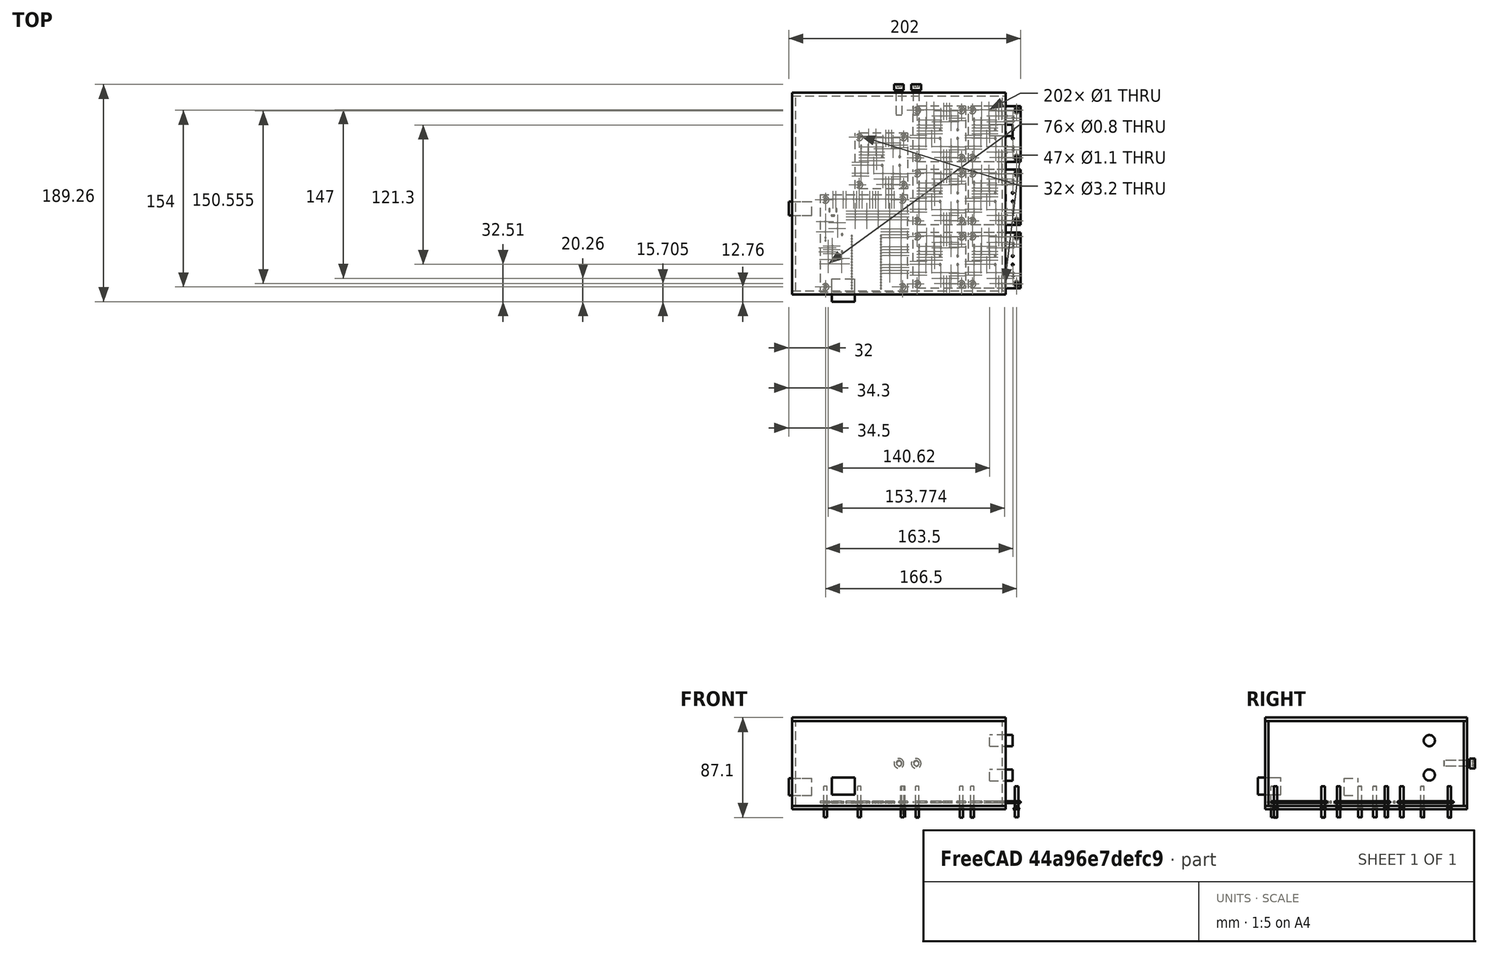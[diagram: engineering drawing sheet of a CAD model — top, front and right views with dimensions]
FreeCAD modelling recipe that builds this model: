
FCSTD DOCUMENT  (FreeCAD 0.20R29177 +426 (Git))
Label: electronics_enclosure
License: All rights reserved
LicenseURL: http://en.wikipedia.org/wiki/All_rights_reserved
objects: Part::Feature×74, Part::Cylinder×35, App::LinkGroup×15, Part::Compound×12, Part::FeaturePython×2, Part::Box×2, Part::MultiFuse×1
note: 126 computed .brp shape members not serialized (recipe doc carries the construction recipe); baked Part::Feature solids carry a one-line shape summary decoded from their .brp

FEATURE [Part::Feature] Pcb_e13b
  Placement = pos=(0,112.5,0) rot=(0,0,1;0rad)
  shape: bbox 45.5 x 48.5 x 1.6 mm, 54 faces (baked)
FEATURE [Part::Feature] Pcb_e13b001
  Placement = pos=(0,57.5,0) rot=(0,0,1;0rad)
  shape: bbox 45.5 x 48.5 x 1.6 mm, 54 faces (baked)
FEATURE [Part::Feature] Pcb_e13b002
  Placement = pos=(0,2.5,0) rot=(0,0,1;0rad)
  shape: bbox 45.5 x 48.5 x 1.6 mm, 54 faces (baked)
FEATURE [Part::Feature] Pcb_b27c
  Placement = pos=(242,-190,0) rot=(0,0,1;3.14159rad)
  shape: bbox 76 x 85 x 1.6 mm, 143 faces (baked)
FEATURE [Part::Compound] Compound  label="PCBs_Compound"
  Links = -> [Pcb_e13b,Pcb_e13b001,Pcb_e13b002,Pcb_b27c]
  Placement = pos=(-99.5,44,-33) rot=(0,0,1;0rad)
FEATURE [Part::Feature] BOLTS_part008  label="Hex socket countersunk head screw DIN 7991 M3 20.008"
  Placement = pos=(16,-79,-40) rot=(0,0,1;0rad)
  shape: bbox 6 x 6 x 20 mm, 12 faces (baked)
FEATURE [Part::Feature] BOLTS_part009  label="Hex socket countersunk head screw DIN 7991 M3 20.009"
  Placement = pos=(16,-37.5,-40) rot=(0,0,1;0rad)
  shape: bbox 6 x 6 x 20 mm, 12 faces (baked)
FEATURE [Part::Feature] BOLTS_part010  label="Hex socket countersunk head screw DIN 7991 M3 20.010"
  Placement = pos=(54.5,-37.5,-40) rot=(0,0,1;0rad)
  shape: bbox 6 x 6 x 20 mm, 12 faces (baked)
FEATURE [Part::Feature] BOLTS_part011  label="Hex socket countersunk head screw DIN 7991 M3 20.011"
  Placement = pos=(54.5,-79,-40) rot=(0,0,1;0rad)
  shape: bbox 6 x 6 x 20 mm, 12 faces (baked)
FEATURE [Part::Compound] Compound003  label="sol_driver_screw_Compound002"
  Links = -> [BOLTS_part008,BOLTS_part009,BOLTS_part010,BOLTS_part011]
FEATURE [Part::Feature] BOLTS_part012  label="Hex socket countersunk head screw DIN 7991 M3 20.012"
  Placement = pos=(16,-79,-40) rot=(0,0,1;0rad)
  shape: bbox 6 x 6 x 20 mm, 12 faces (baked)
FEATURE [Part::Feature] BOLTS_part013  label="Hex socket countersunk head screw DIN 7991 M3 20.013"
  Placement = pos=(16,-37.5,-40) rot=(0,0,1;0rad)
  shape: bbox 6 x 6 x 20 mm, 12 faces (baked)
FEATURE [Part::Feature] BOLTS_part014  label="Hex socket countersunk head screw DIN 7991 M3 20.014"
  Placement = pos=(54.5,-37.5,-40) rot=(0,0,1;0rad)
  shape: bbox 6 x 6 x 20 mm, 12 faces (baked)
FEATURE [Part::Feature] BOLTS_part015  label="Hex socket countersunk head screw DIN 7991 M3 20.015"
  Placement = pos=(54.5,-79,-40) rot=(0,0,1;0rad)
  shape: bbox 6 x 6 x 20 mm, 12 faces (baked)
FEATURE [Part::Feature] BOLTS_part016  label="Hex socket countersunk head screw DIN 7991 M3 20.016"
  Placement = pos=(16,-79,-40) rot=(0,0,1;0rad)
  shape: bbox 6 x 6 x 20 mm, 12 faces (baked)
FEATURE [Part::Feature] BOLTS_part017  label="Hex socket countersunk head screw DIN 7991 M3 20.017"
  Placement = pos=(16,-37.5,-40) rot=(0,0,1;0rad)
  shape: bbox 6 x 6 x 20 mm, 12 faces (baked)
FEATURE [Part::Feature] BOLTS_part018  label="Hex socket countersunk head screw DIN 7991 M3 20.018"
  Placement = pos=(54.5,-37.5,-40) rot=(0,0,1;0rad)
  shape: bbox 6 x 6 x 20 mm, 12 faces (baked)
FEATURE [Part::Feature] BOLTS_part019  label="Hex socket countersunk head screw DIN 7991 M3 20.019"
  Placement = pos=(54.5,-79,-40) rot=(0,0,1;0rad)
  shape: bbox 6 x 6 x 20 mm, 12 faces (baked)
FEATURE [Part::Feature] BOLTS_part020  label="Hex socket countersunk head screw DIN 7991 M3 20.020"
  Placement = pos=(16,-79,-40) rot=(0,0,1;0rad)
  shape: bbox 6 x 6 x 20 mm, 12 faces (baked)
FEATURE [Part::Feature] BOLTS_part021  label="Hex socket countersunk head screw DIN 7991 M3 20.021"
  Placement = pos=(16,-37.5,-40) rot=(0,0,1;0rad)
  shape: bbox 6 x 6 x 20 mm, 12 faces (baked)
FEATURE [Part::Feature] BOLTS_part022  label="Hex socket countersunk head screw DIN 7991 M3 20.022"
  Placement = pos=(54.5,-37.5,-40) rot=(0,0,1;0rad)
  shape: bbox 6 x 6 x 20 mm, 12 faces (baked)
FEATURE [Part::Feature] BOLTS_part023  label="Hex socket countersunk head screw DIN 7991 M3 20.023"
  Placement = pos=(54.5,-79,-40) rot=(0,0,1;0rad)
  shape: bbox 6 x 6 x 20 mm, 12 faces (baked)
FEATURE [Part::Compound] Compound005  label="sol_driver_screw_Compound003"
  Links = -> [BOLTS_part012,BOLTS_part013,BOLTS_part014,BOLTS_part015]
  Placement = pos=(0,110,0) rot=(0,0,1;0rad)
FEATURE [Part::Compound] Compound006  label="sol_driver_screw_Compound004"
  Links = -> [BOLTS_part016,BOLTS_part017,BOLTS_part018,BOLTS_part019]
  Placement = pos=(0,55,0) rot=(0,0,1;0rad)
FEATURE [Part::Compound] Compound007  label="sol_driver_screw_Compound005"
  Links = -> [BOLTS_part020,BOLTS_part021,BOLTS_part022,BOLTS_part023]
FEATURE [Part::Feature] Pcb_e13b003
  Placement = pos=(0,112.5,0) rot=(0,0,1;0rad)
  shape: bbox 45.5 x 48.5 x 1.6 mm, 54 faces (baked)
FEATURE [Part::Feature] Pcb_e13b004
  Placement = pos=(0,57.5,0) rot=(0,0,1;0rad)
  shape: bbox 45.5 x 48.5 x 1.6 mm, 54 faces (baked)
FEATURE [Part::Feature] Pcb_e13b005
  Placement = pos=(0,2.5,0) rot=(0,0,1;0rad)
  shape: bbox 45.5 x 48.5 x 1.6 mm, 54 faces (baked)
FEATURE [Part::Compound] Compound004  label="PCBs_Compound001"
  Links = -> [Pcb_e13b003,Pcb_e13b004,Pcb_e13b005]
  Placement = pos=(-99.5,44,-33) rot=(0,0,1;0rad)
FEATURE [Part::Compound] Compound008
  Links = -> [Compound007,Compound004,Compound005,Compound006]
  Placement = pos=(48,0,0) rot=(0,0,1;0rad)
FEATURE [Part::Feature] BOLTS_part004  label="Hex socket countersunk head screw DIN 7991 M3 20.004"
  Placement = pos=(16,-79,-40) rot=(0,0,1;0rad)
  shape: bbox 6 x 6 x 20 mm, 12 faces (baked)
FEATURE [Part::Feature] BOLTS_part005  label="Hex socket countersunk head screw DIN 7991 M3 20.005"
  Placement = pos=(16,-37.5,-40) rot=(0,0,1;0rad)
  shape: bbox 6 x 6 x 20 mm, 12 faces (baked)
FEATURE [Part::Feature] BOLTS_part006  label="Hex socket countersunk head screw DIN 7991 M3 20.006"
  Placement = pos=(54.5,-37.5,-40) rot=(0,0,1;0rad)
  shape: bbox 6 x 6 x 20 mm, 12 faces (baked)
FEATURE [Part::Feature] BOLTS_part007  label="Hex socket countersunk head screw DIN 7991 M3 20.007"
  Placement = pos=(54.5,-79,-40) rot=(0,0,1;0rad)
  shape: bbox 6 x 6 x 20 mm, 12 faces (baked)
FEATURE [Part::Compound] Compound002  label="sol_driver_screw_Compound001"
  Links = -> [BOLTS_part004,BOLTS_part005,BOLTS_part006,BOLTS_part007]
  Placement = pos=(0,55,0) rot=(0,0,1;0rad)
FEATURE [Part::Feature] BOLTS_part003  label="Hex socket countersunk head screw DIN 7991 M3 20.003"
  Placement = pos=(54.5,-79,-40) rot=(0,0,1;0rad)
  shape: bbox 6 x 6 x 20 mm, 12 faces (baked)
FEATURE [Part::Feature] BOLTS_part002  label="Hex socket countersunk head screw DIN 7991 M3 20.002"
  Placement = pos=(54.5,-37.5,-40) rot=(0,0,1;0rad)
  shape: bbox 6 x 6 x 20 mm, 12 faces (baked)
FEATURE [Part::Feature] BOLTS_part001  label="Hex socket countersunk head screw DIN 7991 M3 20.001"
  Placement = pos=(16,-37.5,-40) rot=(0,0,1;0rad)
  shape: bbox 6 x 6 x 20 mm, 12 faces (baked)
FEATURE [Part::Feature] BOLTS_part  label="Hex socket countersunk head screw DIN 7991 M3 20.0"
  Placement = pos=(16,-79,-40) rot=(0,0,1;0rad)
  shape: bbox 6 x 6 x 20 mm, 12 faces (baked)
FEATURE [Part::Compound] Compound001  label="sol_driver_screw_Compound"
  Links = -> [BOLTS_part,BOLTS_part001,BOLTS_part002,BOLTS_part003]
  Placement = pos=(0,110,0) rot=(0,0,1;0rad)
FEATURE [Part::Feature] BOLTS_part024  label="Hex socket countersunk head screw DIN 7991 M3 20.024"
  Placement = pos=(16,-79,-40) rot=(0,0,1;0rad)
  shape: bbox 6 x 6 x 20 mm, 12 faces (baked)
FEATURE [Part::Feature] BOLTS_part025  label="Hex socket countersunk head screw DIN 7991 M3 20.025"
  Placement = pos=(16,-37.5,-40) rot=(0,0,1;0rad)
  shape: bbox 6 x 6 x 20 mm, 12 faces (baked)
FEATURE [Part::Feature] BOLTS_part026  label="Hex socket countersunk head screw DIN 7991 M3 20.026"
  Placement = pos=(54.5,-37.5,-40) rot=(0,0,1;0rad)
  shape: bbox 6 x 6 x 20 mm, 12 faces (baked)
FEATURE [Part::Feature] BOLTS_part027  label="Hex socket countersunk head screw DIN 7991 M3 20.027"
  Placement = pos=(54.5,-79,-40) rot=(0,0,1;0rad)
  shape: bbox 6 x 6 x 20 mm, 12 faces (baked)
FEATURE [Part::Compound] Compound009  label="sol_driver_screw_Compound006"
  Links = -> [BOLTS_part024,BOLTS_part025,BOLTS_part026,BOLTS_part027]
FEATURE [Part::Feature] BOLTS_part028  label="Hex socket countersunk head screw DIN 7991 M3 20.028"
  Placement = pos=(3,-81.5,-53) rot=(0,0,1;0rad)
  shape: bbox 6 x 6 x 20 mm, 12 faces (baked)
FEATURE [Part::Feature] BOLTS_part029  label="Hex socket countersunk head screw DIN 7991 M3 20.029"
  Placement = pos=(3,-5.5,-53) rot=(0,0,1;0rad)
  shape: bbox 6 x 6 x 20 mm, 12 faces (baked)
FEATURE [Part::Feature] BOLTS_part030  label="Hex socket countersunk head screw DIN 7991 M3 20.030"
  Placement = pos=(-64,-81.5,-53) rot=(0,0,1;0rad)
  shape: bbox 6 x 6 x 20 mm, 12 faces (baked)
FEATURE [Part::Feature] BOLTS_part031  label="Hex socket countersunk head screw DIN 7991 M3 20.031"
  Placement = pos=(-64,-5.5,-53) rot=(0,0,1;0rad)
  shape: bbox 6 x 6 x 20 mm, 12 faces (baked)
FEATURE [Part::Compound] Compound010
  Links = -> [BOLTS_part028,BOLTS_part029,BOLTS_part030,BOLTS_part031]
  Placement = pos=(0,0,13) rot=(0,0,1;0rad)
FEATURE [Part::Feature] Pcb_e13b006
  Placement = pos=(-150,133,-33) rot=(0,0,1;0rad)
  shape: bbox 45.5 x 48.5 x 1.6 mm, 54 faces (baked)
FEATURE [Part::Feature] BOLTS_part032  label="Hex socket countersunk head screw DIN 7991 M3 20.032"
  Placement = pos=(16,-79,-40) rot=(0,0,1;0rad)
  shape: bbox 6 x 6 x 20 mm, 12 faces (baked)
FEATURE [Part::Feature] BOLTS_part033  label="Hex socket countersunk head screw DIN 7991 M3 20.033"
  Placement = pos=(16,-37.5,-40) rot=(0,0,1;0rad)
  shape: bbox 6 x 6 x 20 mm, 12 faces (baked)
FEATURE [Part::Feature] BOLTS_part034  label="Hex socket countersunk head screw DIN 7991 M3 20.034"
  Placement = pos=(54.5,-37.5,-40) rot=(0,0,1;0rad)
  shape: bbox 6 x 6 x 20 mm, 12 faces (baked)
FEATURE [Part::Feature] BOLTS_part035  label="Hex socket countersunk head screw DIN 7991 M3 20.035"
  Placement = pos=(54.5,-79,-40) rot=(0,0,1;0rad)
  shape: bbox 6 x 6 x 20 mm, 12 faces (baked)
FEATURE [Part::Compound] Compound011  label="sol_driver_screw_Compound007"
  Links = -> [BOLTS_part032,BOLTS_part033,BOLTS_part034,BOLTS_part035]
  Placement = pos=(-50.5,86.5,0) rot=(0,0,1;0rad)
FEATURE [Part::Feature] face_panel
  shape: bbox 186 x 3 x 74 mm, 6 faces (baked)
FEATURE [Part::Feature] behind_panel
  Placement = pos=(0,-173,0) rot=(0,0,1;0rad)
  shape: bbox 186 x 3 x 74 mm, 6 faces (baked)
FEATURE [Part::Feature] left_panel
  shape: bbox 3 x 170 x 74 mm, 6 faces (baked)
FEATURE [Part::Feature] right_panel
  Placement = pos=(-183,0,0) rot=(0,0,1;0rad)
  shape: bbox 3 x 170 x 74 mm, 6 faces (baked)
FEATURE [Part::Feature] bottom_panel
  shape: bbox 186 x 176 x 3 mm, 6 faces (baked)
FEATURE [Part::Feature] top_panel
  shape: bbox 186 x 176 x 3 mm, 6 faces (baked)
FEATURE [Part::FeaturePython] Box  # WARN: FeaturePython — macro-defined, semantics opaque (R4)
  parts = -> [face_panel,behind_panel,left_panel,right_panel,bottom_panel,top_panel]
FEATURE [Part::Box] Box001  label="Cube"
  AttacherType = Attacher::AttachEngine3D
  Height = 15
  Length = 20
  Placement = pos=(-58.5,-94.26,-27.17) rot=(0,0,1;0rad)
  Width = 20
FEATURE [Part::Box] Box002  label="Cube001"
  AttacherType = Attacher::AttachEngine3D
  Height = 15
  Length = 20
  Placement = pos=(-96,-19,-28) rot=(0,0,1;0rad)
  Width = 12
FEATURE [Part::Feature] BOLTS_part036  label="Hex socket head cap screw DIN 912 M5 20.0"
  Placement = pos=(15,95,0) rot=(1,0,0;1.5708rad)
  shape: bbox 8.5 x 27 x 8.5 mm, 12 faces (baked)
FEATURE [Part::Feature] BOLTS_part037  label="Hex socket head cap screw DIN 912 M5 20.001"
  Placement = pos=(0,95,0) rot=(1,0,0;1.5708rad)
  shape: bbox 8.5 x 27 x 8.5 mm, 12 faces (baked)
FEATURE [App::LinkGroup] LinkGroup001  label="banana_plugs1"
  ElementList = -> [BOLTS_part036,BOLTS_part037]
  LinkMode = 0
FEATURE [Part::Feature] BOLTS_part038  label="Hex socket head cap screw DIN 912 M5 20.002"
  Placement = pos=(15,95,0) rot=(1,0,0;1.5708rad)
  shape: bbox 8.5 x 27 x 8.5 mm, 12 faces (baked)
FEATURE [Part::Feature] BOLTS_part039  label="Hex socket head cap screw DIN 912 M5 20.003"
  Placement = pos=(0,95,0) rot=(1,0,0;1.5708rad)
  shape: bbox 8.5 x 27 x 8.5 mm, 12 faces (baked)
FEATURE [App::LinkGroup] LinkGroup002  label="banana_plugs002"
  ElementList = -> [BOLTS_part038,BOLTS_part039]
  LinkMode = 0
  Placement = pos=(35,0,0) rot=(0,0,1;0rad)
FEATURE [Part::Feature] BOLTS_part040  label="Hex socket head cap screw DIN 912 M5 20.004"
  Placement = pos=(15,95,0) rot=(1,0,0;1.5708rad)
  shape: bbox 8.5 x 27 x 8.5 mm, 12 faces (baked)
FEATURE [Part::Feature] BOLTS_part041  label="Hex socket head cap screw DIN 912 M5 20.005"
  Placement = pos=(0,95,0) rot=(1,0,0;1.5708rad)
  shape: bbox 8.5 x 27 x 8.5 mm, 12 faces (baked)
FEATURE [App::LinkGroup] LinkGroup003  label="banana_plugs003"
  ElementList = -> [BOLTS_part040,BOLTS_part041]
  LinkMode = 0
  Placement = pos=(35,0,-13) rot=(0,0,1;0rad)
FEATURE [Part::Feature] BOLTS_part042  label="Hex socket head cap screw DIN 912 M5 20.006"
  Placement = pos=(15,95,0) rot=(1,0,0;1.5708rad)
  shape: bbox 8.5 x 27 x 8.5 mm, 12 faces (baked)
FEATURE [Part::Feature] BOLTS_part043  label="Hex socket head cap screw DIN 912 M5 20.007"
  Placement = pos=(0,95,0) rot=(1,0,0;1.5708rad)
  shape: bbox 8.5 x 27 x 8.5 mm, 12 faces (baked)
FEATURE [App::LinkGroup] LinkGroup004  label="banana_plugs004"
  ElementList = -> [BOLTS_part042,BOLTS_part043]
  LinkMode = 0
  Placement = pos=(0,0,-13) rot=(0,0,1;0rad)
FEATURE [Part::Feature] BOLTS_part044  label="Hex socket head cap screw DIN 912 M5 20.008"
  Placement = pos=(15,95,0) rot=(1,0,0;1.5708rad)
  shape: bbox 8.5 x 27 x 8.5 mm, 12 faces (baked)
FEATURE [Part::Feature] BOLTS_part045  label="Hex socket head cap screw DIN 912 M5 20.009"
  Placement = pos=(0,95,0) rot=(1,0,0;1.5708rad)
  shape: bbox 8.5 x 27 x 8.5 mm, 12 faces (baked)
FEATURE [App::LinkGroup] LinkGroup005  label="banana_plugs005"
  ElementList = -> [BOLTS_part044,BOLTS_part045]
  LinkMode = 0
  Placement = pos=(-35,0,0) rot=(0,0,1;0rad)
FEATURE [Part::Feature] BOLTS_part046  label="Hex socket head cap screw DIN 912 M5 20.010"
  Placement = pos=(15,95,0) rot=(1,0,0;1.5708rad)
  shape: bbox 8.5 x 27 x 8.5 mm, 12 faces (baked)
FEATURE [Part::Feature] BOLTS_part047  label="Hex socket head cap screw DIN 912 M5 20.011"
  Placement = pos=(0,95,0) rot=(1,0,0;1.5708rad)
  shape: bbox 8.5 x 27 x 8.5 mm, 12 faces (baked)
FEATURE [App::LinkGroup] LinkGroup006  label="banana_plugs006"
  ElementList = -> [BOLTS_part046,BOLTS_part047]
  LinkMode = 0
  Placement = pos=(-35,0,-13) rot=(0,0,1;0rad)
FEATURE [App::LinkGroup] LinkGroup007
  ElementList = -> [LinkGroup001,LinkGroup002,LinkGroup003,LinkGroup004,LinkGroup005,LinkGroup006]
  LinkMode = 0
  Placement = pos=(4,-10,26) rot=(0,0,1;-1.5708rad)
FEATURE [Part::Feature] BOLTS_part048  label="Hex socket head cap screw DIN 912 M5 20.012"
  Placement = pos=(15,95,0) rot=(1,0,0;1.5708rad)
  shape: bbox 8.5 x 27 x 8.5 mm, 12 faces (baked)
FEATURE [Part::Feature] BOLTS_part049  label="Hex socket head cap screw DIN 912 M5 20.013"
  Placement = pos=(0,95,0) rot=(1,0,0;1.5708rad)
  shape: bbox 8.5 x 27 x 8.5 mm, 12 faces (baked)
FEATURE [Part::Feature] BOLTS_part050  label="Hex socket head cap screw DIN 912 M5 20.014"
  Placement = pos=(15,95,0) rot=(1,0,0;1.5708rad)
  shape: bbox 8.5 x 27 x 8.5 mm, 12 faces (baked)
FEATURE [Part::Feature] BOLTS_part051  label="Hex socket head cap screw DIN 912 M5 20.015"
  Placement = pos=(0,95,0) rot=(1,0,0;1.5708rad)
  shape: bbox 8.5 x 27 x 8.5 mm, 12 faces (baked)
FEATURE [Part::Feature] BOLTS_part052  label="Hex socket head cap screw DIN 912 M5 20.016"
  Placement = pos=(15,95,0) rot=(1,0,0;1.5708rad)
  shape: bbox 8.5 x 27 x 8.5 mm, 12 faces (baked)
FEATURE [Part::Feature] BOLTS_part053  label="Hex socket head cap screw DIN 912 M5 20.017"
  Placement = pos=(0,95,0) rot=(1,0,0;1.5708rad)
  shape: bbox 8.5 x 27 x 8.5 mm, 12 faces (baked)
FEATURE [Part::Feature] BOLTS_part054  label="Hex socket head cap screw DIN 912 M5 20.018"
  Placement = pos=(15,95,0) rot=(1,0,0;1.5708rad)
  shape: bbox 8.5 x 27 x 8.5 mm, 12 faces (baked)
FEATURE [Part::Feature] BOLTS_part055  label="Hex socket head cap screw DIN 912 M5 20.019"
  Placement = pos=(0,95,0) rot=(1,0,0;1.5708rad)
  shape: bbox 8.5 x 27 x 8.5 mm, 12 faces (baked)
FEATURE [Part::Feature] BOLTS_part056  label="Hex socket head cap screw DIN 912 M5 20.020"
  Placement = pos=(15,95,0) rot=(1,0,0;1.5708rad)
  shape: bbox 8.5 x 27 x 8.5 mm, 12 faces (baked)
FEATURE [Part::Feature] BOLTS_part057  label="Hex socket head cap screw DIN 912 M5 20.021"
  Placement = pos=(0,95,0) rot=(1,0,0;1.5708rad)
  shape: bbox 8.5 x 27 x 8.5 mm, 12 faces (baked)
FEATURE [Part::Feature] BOLTS_part058  label="Hex socket head cap screw DIN 912 M5 20.022"
  Placement = pos=(15,95,0) rot=(1,0,0;1.5708rad)
  shape: bbox 8.5 x 27 x 8.5 mm, 12 faces (baked)
FEATURE [Part::Feature] BOLTS_part059  label="Hex socket head cap screw DIN 912 M5 20.023"
  Placement = pos=(0,95,0) rot=(1,0,0;1.5708rad)
  shape: bbox 8.5 x 27 x 8.5 mm, 12 faces (baked)
FEATURE [App::LinkGroup] LinkGroup008  label="banana_plugs007"
  ElementList = -> [BOLTS_part048,BOLTS_part049]
  LinkMode = 0
FEATURE [App::LinkGroup] LinkGroup009  label="banana_plugs008"
  ElementList = -> [BOLTS_part050,BOLTS_part051]
  LinkMode = 0
  Placement = pos=(35,0,0) rot=(0,0,1;0rad)
FEATURE [App::LinkGroup] LinkGroup010  label="banana_plugs009"
  ElementList = -> [BOLTS_part052,BOLTS_part053]
  LinkMode = 0
  Placement = pos=(35,0,-13) rot=(0,0,1;0rad)
FEATURE [App::LinkGroup] LinkGroup011  label="banana_plugs010"
  ElementList = -> [BOLTS_part054,BOLTS_part055]
  LinkMode = 0
  Placement = pos=(0,0,-13) rot=(0,0,1;0rad)
FEATURE [App::LinkGroup] LinkGroup012  label="banana_plugs011"
  ElementList = -> [BOLTS_part056,BOLTS_part057]
  LinkMode = 0
  Placement = pos=(-35,0,0) rot=(0,0,1;0rad)
FEATURE [App::LinkGroup] LinkGroup013  label="banana_plugs012"
  ElementList = -> [BOLTS_part058,BOLTS_part059]
  LinkMode = 0
  Placement = pos=(-35,0,-13) rot=(0,0,1;0rad)
FEATURE [App::LinkGroup] LinkGroup014
  ElementList = -> [LinkGroup008,LinkGroup009,LinkGroup010,LinkGroup011,LinkGroup012,LinkGroup013]
  LinkMode = 0
  Placement = pos=(4,-10,-4) rot=(0,0,1;-1.5708rad)
FEATURE [Part::Cylinder] Cylinder
  Angle = 360
  AttacherType = Attacher::AttachEngine3D
  FirstAngle = 0
  Height = 20
  Placement = pos=(79,55,-10.12) rot=(0,1,0;1.5708rad)
  Radius = 4.88
  SecondAngle = 0
FEATURE [Part::Cylinder] Cylinder001
  Angle = 360
  AttacherType = Attacher::AttachEngine3D
  FirstAngle = 0
  Height = 20
  Placement = pos=(79,55,19.88) rot=(0,1,0;1.5708rad)
  Radius = 4.88
  SecondAngle = 0
FEATURE [Part::Cylinder] Cylinder002
  Angle = 360
  AttacherType = Attacher::AttachEngine3D
  FirstAngle = 0
  Height = 10
  Placement = pos=(82,74.5,-47) rot=(0,0,1;0rad)
  Radius = 1.5
  SecondAngle = 0
FEATURE [Part::Cylinder] Cylinder004
  Angle = 360
  AttacherType = Attacher::AttachEngine3D
  FirstAngle = 0
  Height = 10
  Placement = pos=(82,33,-47) rot=(0,0,1;0rad)
  Radius = 1.5
  SecondAngle = 0
FEATURE [Part::Cylinder] Cylinder005
  Angle = 360
  AttacherType = Attacher::AttachEngine3D
  FirstAngle = 0
  Height = 10
  Placement = pos=(43.5,33,-47) rot=(0,0,1;0rad)
  Radius = 1.5
  SecondAngle = 0
FEATURE [Part::Cylinder] Cylinder006
  Angle = 360
  AttacherType = Attacher::AttachEngine3D
  FirstAngle = 0
  Height = 10
  Placement = pos=(82,19.5,-47) rot=(0,0,1;0rad)
  Radius = 1.5
  SecondAngle = 0
FEATURE [Part::Cylinder] Cylinder007
  Angle = 360
  AttacherType = Attacher::AttachEngine3D
  FirstAngle = 0
  Height = 10
  Placement = pos=(43.5,19.5,-47) rot=(0,0,1;0rad)
  Radius = 1.5
  SecondAngle = 0
FEATURE [Part::Cylinder] Cylinder008
  Angle = 360
  AttacherType = Attacher::AttachEngine3D
  FirstAngle = 0
  Height = 10
  Placement = pos=(82,-22,-47) rot=(0,0,1;0rad)
  Radius = 1.5
  SecondAngle = 0
FEATURE [Part::Cylinder] Cylinder009
  Angle = 360
  AttacherType = Attacher::AttachEngine3D
  FirstAngle = 0
  Height = 10
  Placement = pos=(43.5,-22,-47) rot=(0,0,1;0rad)
  Radius = 1.5
  SecondAngle = 0
FEATURE [Part::Cylinder] Cylinder010
  Angle = 360
  AttacherType = Attacher::AttachEngine3D
  FirstAngle = 0
  Height = 10
  Placement = pos=(82,-35.5,-47) rot=(0,0,1;0rad)
  Radius = 1.5
  SecondAngle = 0
FEATURE [Part::Cylinder] Cylinder012
  Angle = 360
  AttacherType = Attacher::AttachEngine3D
  FirstAngle = 0
  Height = 10
  Placement = pos=(43.5,-77,-47) rot=(0,0,1;0rad)
  Radius = 1.5
  SecondAngle = 0
FEATURE [Part::Cylinder] Cylinder013
  Angle = 360
  AttacherType = Attacher::AttachEngine3D
  FirstAngle = 0
  Height = 10
  Placement = pos=(82,-77,-47) rot=(0,0,1;0rad)
  Radius = 1.5
  SecondAngle = 0
FEATURE [Part::Cylinder] Cylinder014
  Angle = 360
  AttacherType = Attacher::AttachEngine3D
  FirstAngle = 0
  Height = 10
  Placement = pos=(43.5,-35.5,-47) rot=(0,0,1;0rad)
  Radius = 1.5
  SecondAngle = 0
FEATURE [Part::Cylinder] Cylinder015
  Angle = 360
  AttacherType = Attacher::AttachEngine3D
  FirstAngle = 0
  Height = 10
  Placement = pos=(34,-22,-47) rot=(0,0,1;0rad)
  Radius = 1.5
  SecondAngle = 0
FEATURE [Part::Cylinder] Cylinder016
  Angle = 360
  AttacherType = Attacher::AttachEngine3D
  FirstAngle = 0
  Height = 10
  Placement = pos=(-4.5,-77,-47) rot=(0,0,1;0rad)
  Radius = 1.5
  SecondAngle = 0
FEATURE [Part::Cylinder] Cylinder017
  Angle = 360
  AttacherType = Attacher::AttachEngine3D
  FirstAngle = 0
  Height = 10
  Placement = pos=(-17.5,-3.5,-47) rot=(0,0,1;0rad)
  Radius = 1.5
  SecondAngle = 0
FEATURE [Part::Cylinder] Cylinder018
  Angle = 360
  AttacherType = Attacher::AttachEngine3D
  FirstAngle = 0
  Height = 10
  Placement = pos=(-4.5,-22,-47) rot=(0,0,1;0rad)
  Radius = 1.5
  SecondAngle = 0
FEATURE [Part::Cylinder] Cylinder019
  Angle = 360
  AttacherType = Attacher::AttachEngine3D
  FirstAngle = 0
  Height = 10
  Placement = pos=(-17.5,-79.5,-47) rot=(0,0,1;0rad)
  Radius = 1.5
  SecondAngle = 0
FEATURE [Part::Cylinder] Cylinder020
  Angle = 360
  AttacherType = Attacher::AttachEngine3D
  FirstAngle = 0
  Height = 10
  Placement = pos=(34,19.5,-47) rot=(0,0,1;0rad)
  Radius = 1.5
  SecondAngle = 0
FEATURE [Part::Cylinder] Cylinder021
  Angle = 360
  AttacherType = Attacher::AttachEngine3D
  FirstAngle = 0
  Height = 10
  Placement = pos=(-16.5,9.5,-47) rot=(0,0,1;0rad)
  Radius = 1.5
  SecondAngle = 0
FEATURE [Part::Cylinder] Cylinder022
  Angle = 360
  AttacherType = Attacher::AttachEngine3D
  FirstAngle = 0
  Height = 10
  Placement = pos=(-84.5,-79.5,-47) rot=(0,0,1;0rad)
  Radius = 1.5
  SecondAngle = 0
FEATURE [Part::Cylinder] Cylinder023
  Angle = 360
  AttacherType = Attacher::AttachEngine3D
  FirstAngle = 0
  Height = 10
  Placement = pos=(-4.5,19.5,-47) rot=(0,0,1;0rad)
  Radius = 1.5
  SecondAngle = 0
FEATURE [Part::Cylinder] Cylinder024
  Angle = 360
  AttacherType = Attacher::AttachEngine3D
  FirstAngle = 0
  Height = 10
  Placement = pos=(-4.5,33,-47) rot=(0,0,1;0rad)
  Radius = 1.5
  SecondAngle = 0
FEATURE [Part::Cylinder] Cylinder025
  Angle = 360
  AttacherType = Attacher::AttachEngine3D
  FirstAngle = 0
  Height = 10
  Placement = pos=(34,33,-47) rot=(0,0,1;0rad)
  Radius = 1.5
  SecondAngle = 0
FEATURE [Part::Cylinder] Cylinder026
  Angle = 360
  AttacherType = Attacher::AttachEngine3D
  FirstAngle = 0
  Height = 10
  Placement = pos=(34,74.5,-47) rot=(0,0,1;0rad)
  Radius = 1.5
  SecondAngle = 0
FEATURE [Part::Cylinder] Cylinder027
  Angle = 360
  AttacherType = Attacher::AttachEngine3D
  FirstAngle = 0
  Height = 10
  Placement = pos=(-55,9.5,-47) rot=(0,0,1;0rad)
  Radius = 1.5
  SecondAngle = 0
FEATURE [Part::Cylinder] Cylinder028
  Angle = 360
  AttacherType = Attacher::AttachEngine3D
  FirstAngle = 0
  Height = 10
  Placement = pos=(-84.5,-3.5,-47) rot=(0,0,1;0rad)
  Radius = 1.5
  SecondAngle = 0
FEATURE [Part::Cylinder] Cylinder029
  Angle = 360
  AttacherType = Attacher::AttachEngine3D
  FirstAngle = 0
  Height = 10
  Placement = pos=(-55,51,-47) rot=(0,0,1;0rad)
  Radius = 1.5
  SecondAngle = 0
FEATURE [Part::Cylinder] Cylinder030
  Angle = 360
  AttacherType = Attacher::AttachEngine3D
  FirstAngle = 0
  Height = 10
  Placement = pos=(-16.5,51,-47) rot=(0,0,1;0rad)
  Radius = 1.5
  SecondAngle = 0
FEATURE [Part::Cylinder] Cylinder031
  Angle = 360
  AttacherType = Attacher::AttachEngine3D
  FirstAngle = 0
  Height = 10
  Placement = pos=(-4.5,74.5,-47) rot=(0,0,1;0rad)
  Radius = 1.5
  SecondAngle = 0
FEATURE [Part::Cylinder] Cylinder032
  Angle = 360
  AttacherType = Attacher::AttachEngine3D
  FirstAngle = 0
  Height = 10
  Placement = pos=(-84.5,-3.5,-47) rot=(0,0,1;0rad)
  Radius = 1.5
  SecondAngle = 0
FEATURE [Part::Cylinder] Cylinder033
  Angle = 360
  AttacherType = Attacher::AttachEngine3D
  FirstAngle = 0
  Height = 10
  Placement = pos=(43.5,74.5,-47.1) rot=(0,0,1;0rad)
  Radius = 1.5
  SecondAngle = 0
FEATURE [Part::Cylinder] Cylinder034
  Angle = 360
  AttacherType = Attacher::AttachEngine3D
  FirstAngle = 0
  Height = 10
  Placement = pos=(-4.5,-35.5,-47.1) rot=(0,0,1;0rad)
  Radius = 1.5
  SecondAngle = 0
FEATURE [Part::Cylinder] Cylinder035
  Angle = 360
  AttacherType = Attacher::AttachEngine3D
  FirstAngle = 0
  Height = 10
  Placement = pos=(34,-35.5,-47.1) rot=(0,0,1;0rad)
  Radius = 1.5
  SecondAngle = 0
FEATURE [Part::Cylinder] Cylinder036
  Angle = 360
  AttacherType = Attacher::AttachEngine3D
  FirstAngle = 0
  Height = 10
  Placement = pos=(34,-77,-47.1) rot=(0,0,1;0rad)
  Radius = 1.5
  SecondAngle = 0
FEATURE [Part::MultiFuse] Fusion
  Placement = pos=(20.5,-2,0) rot=(0,0,1;0rad)
  Shapes = -> [Cylinder036,Cylinder002,Cylinder004,Cylinder005,Cylinder006,Cylinder007,Cylinder008,Cylinder009,Cylinder010,Cylinder012,Cylinder013,Cylinder014,Cylinder015,Cylinder016,Cylinder017,Cylinder018,Cylinder019,Cylinder020,Cylinder021,Cylinder022,Cylinder023,Cylinder024,Cylinder025,Cylinder026,Cylinder027,Cylinder028,Cylinder029,Cylinder030,Cylinder031,Cylinder032,Cylinder033,Cylinder034,Cylinder035]
FEATURE [App::LinkGroup] LinkGroup
  ElementList = -> [Compound,Compound001,Compound002,Compound003,Compound008,Compound009,Compound010,Pcb_e13b006,Compound011,Fusion]
  LinkMode = 0
  Placement = pos=(-20.5,2,-0.1) rot=(0,0.999201,0.039968;0rad)
FEATURE [Part::FeaturePython] MultiJoin  # WARN: FeaturePython — macro-defined, semantics opaque (R4)
